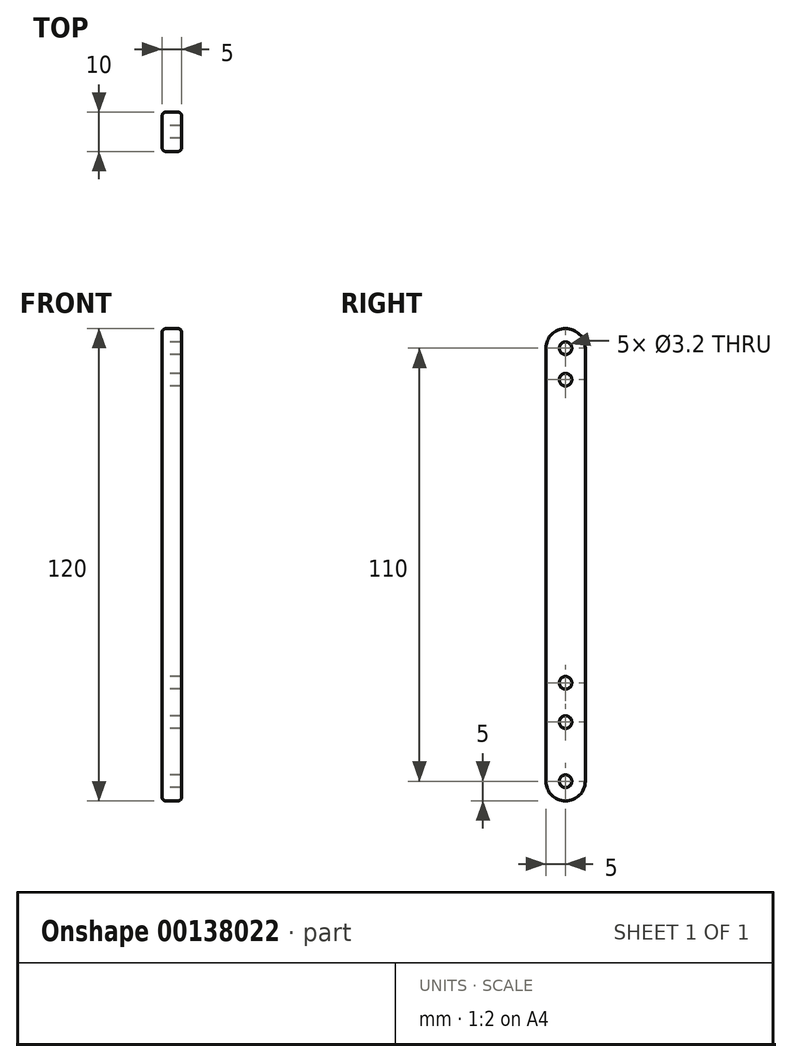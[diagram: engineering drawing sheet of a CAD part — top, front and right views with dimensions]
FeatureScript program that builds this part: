
annotation { "Feature Type Name" : "Feature", "Feature Type Description" : "" }
export const myFeature = defineFeature(function(context is Context, id is Id, definition is map)
    precondition{}
    {
        {
            var Q0;
            Q0=qCreatedBy(makeId("Right.planeOp"),FACE);
            var sketch = newSketch(context, id + "F0", { "sketchPlane" : qUnion([Q0])});
            skLineSegment(sketch, "E0.bottom", {"start": v(-5, 0) * mm, "end": v(5, 0) * mm});
            skLineSegment(sketch, "E0.top", {"start": v(-5, 120) * mm, "end": v(5, 120) * mm});
            skLineSegment(sketch, "E0.left", {"start": v(-5, 0) * mm, "end": v(-5, 120) * mm});
            skLineSegment(sketch, "E0.right", {"start": v(5, 0) * mm, "end": v(5, 120) * mm});
            skLineSegment(sketch, "E1", {"start": v(0, 120) * mm, "end": v(0, 0) * mm, "construction": true});
            skPoint(sketch, "E1.startSnap0", {"position": v(0, 120) * mm});
            skCircle(sketch, "E2", {"center": v(0, 115) * mm, "radius": 1.6 * mm});
            skCircle(sketch, "E3", {"center": v(0, 107) * mm, "radius": 1.6 * mm});
            skCircle(sketch, "E4", {"center": v(0, 5) * mm, "radius": 1.6 * mm});
            skCircle(sketch, "E5", {"center": v(0, 20) * mm, "radius": 1.6 * mm});
            skCircle(sketch, "E6", {"center": v(0, 30) * mm, "radius": 1.6 * mm});
            skSolve(sketch);
        }
        {
            var Q0;
            Q0=makeQuery(id+"F0.imprint","IMPRINT",FACE,{"disambiguationData":[TD([[makeQuery(id+"F0.imprint","IMPRINT",EDGE,{"derivedFrom":sQuery(id+"F0.wireOp",EDGE,"E0.bottom")}),1.0]])]});
            extrude(context, id + "F1", {"entities" : qUnion([Q0]), "depth" : 5 * mm});
        }
        {
            var Q0;
            Q0=makeQuery(id+"F1.opExtrude","SWEPT_EDGE",EDGE,{"disambiguationData":[OSD([sQuery(id+"F0.wireOp",EDGE,"E0.bottom"),sQuery(id+"F0.wireOp",EDGE,"E0.right")])]});
            var Q1;
            Q1=makeQuery(id+"F1.opExtrude","SWEPT_EDGE",EDGE,{"disambiguationData":[OSD([sQuery(id+"F0.wireOp",EDGE,"E0.bottom"),sQuery(id+"F0.wireOp",EDGE,"E0.left")])]});
            var Q2;
            Q2=makeQuery(id+"F1.opExtrude","SWEPT_EDGE",EDGE,{"disambiguationData":[OSD([sQuery(id+"F0.wireOp",EDGE,"E0.top"),sQuery(id+"F0.wireOp",EDGE,"E0.right")])]});
            var Q3;
            Q3=makeQuery(id+"F1.opExtrude","SWEPT_EDGE",EDGE,{"disambiguationData":[OSD([sQuery(id+"F0.wireOp",EDGE,"E0.top"),sQuery(id+"F0.wireOp",EDGE,"E0.left")])]});
            fillet(context, id + "F2", {"entities" : qUnion([Q0, Q1, Q2, Q3]), "radius" : 5 * mm, "tangentPropagation" : true, "allowEdgeOverflow" : false});
        }
        {
            var Q0;
            {var subQ0=sQuery(id+"F0.wireOp",EDGE,"E0.left");var subQ1=sQuery(id+"F0.wireOp",EDGE,"E0.top");Q0=makeQuery(id+"F2.opFillet","BLEND_EDGE",EDGE,{"blendedFrom":[makeQuery(id+"F1.opExtrude","SWEPT_EDGE",EDGE,{"disambiguationData":[OSD([subQ1,subQ0])]}),makeQuery(id+"F1.opExtrude","CAP_FACE",FACE,{"disambiguationData":[OSD([sQuery(id+"F0.wireOp",EDGE,"E0.bottom"),subQ1,subQ0,sQuery(id+"F0.wireOp",EDGE,"E0.right"),sQuery(id+"F0.wireOp",EDGE,"E2"),sQuery(id+"F0.wireOp",EDGE,"E3"),sQuery(id+"F0.wireOp",EDGE,"E4")])],"isStart":false})],"blendedInto":[makeQuery(id+"F1.opExtrude","CAP_FACE",FACE,{"disambiguationData":[OSD([sQuery(id+"F0.wireOp",EDGE,"E0.bottom"),subQ1,subQ0,sQuery(id+"F0.wireOp",EDGE,"E0.right"),sQuery(id+"F0.wireOp",EDGE,"E2"),sQuery(id+"F0.wireOp",EDGE,"E3"),sQuery(id+"F0.wireOp",EDGE,"E4")])],"isStart":false})]});}
            var Q1;
            Q1=makeQuery(id+"F1.opExtrude","CAP_EDGE",EDGE,{"disambiguationData":[OSD([sQuery(id+"F0.wireOp",EDGE,"E0.right")])],"isStart":true});
            fillet(context, id + "F3", {"entities" : qUnion([Q0, Q1]), "radius" : 1 * mm, "tangentPropagation" : true, "allowEdgeOverflow" : false});
        }
    });
